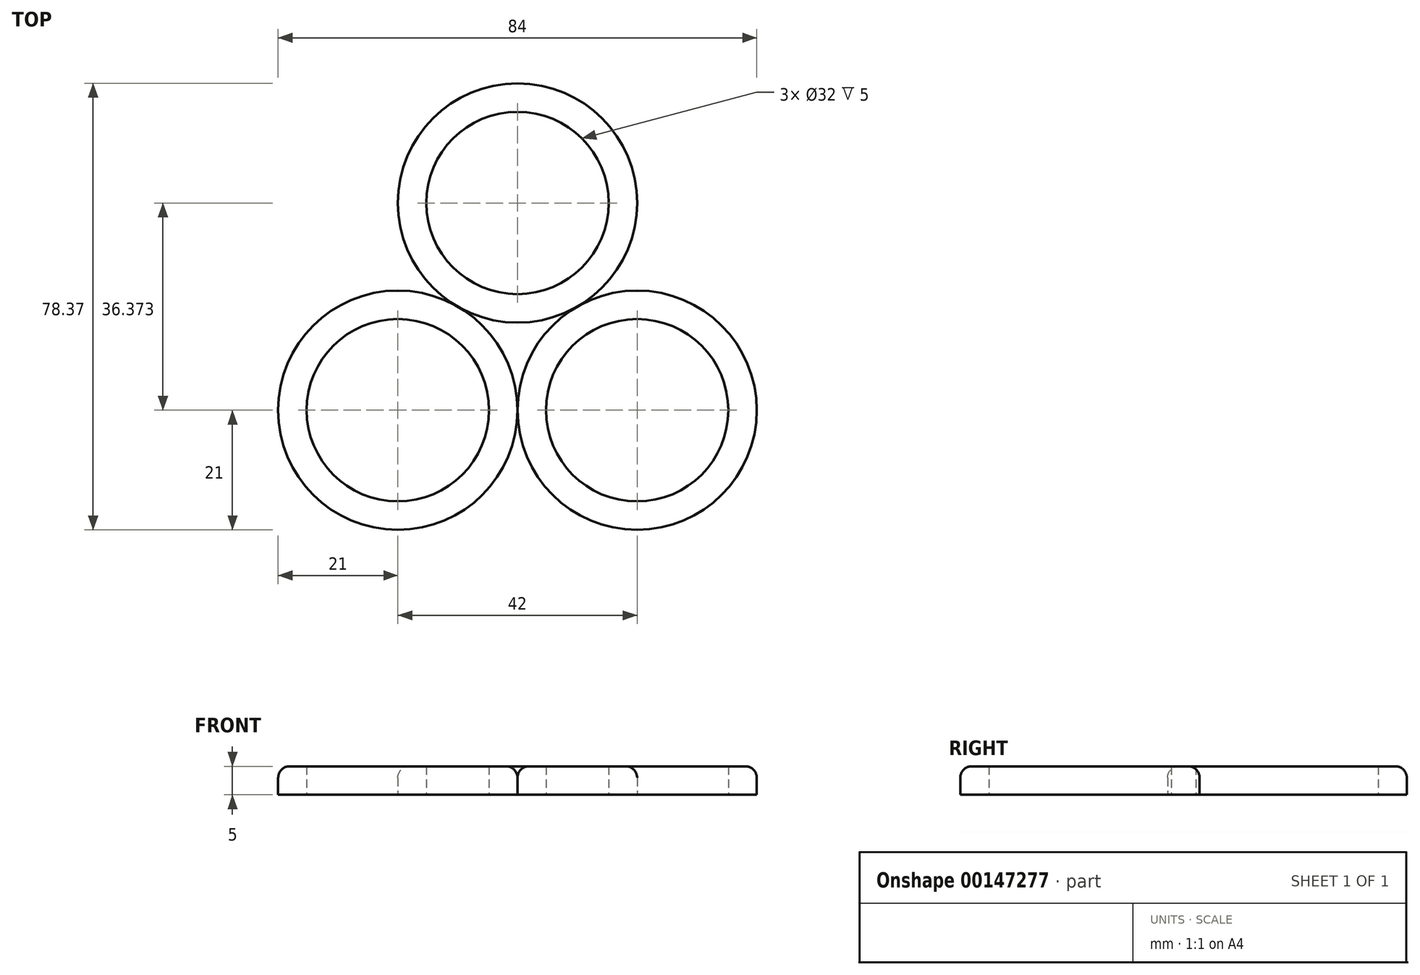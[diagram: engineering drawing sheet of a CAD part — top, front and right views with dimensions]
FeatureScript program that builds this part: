
annotation { "Feature Type Name" : "Feature", "Feature Type Description" : "" }
export const myFeature = defineFeature(function(context is Context, id is Id, definition is map)
    precondition{}
    {
        {
            var Q0;
            Q0=qCreatedBy(makeId("Top.planeOp"),FACE);
            var sketch = newSketch(context, id + "F0", { "sketchPlane" : qUnion([Q0])});
            skCircle(sketch, "E0", {"center": v(0, 0) * mm, "radius": 16 * mm});
            skCircle(sketch, "E1.0", {"center": v(0, 0) * mm, "radius": 21 * mm});
            skCircle(sketch, "E2", {"center": v(-42, 0) * mm, "radius": 16 * mm});
            skCircle(sketch, "E3.0", {"center": v(-42, 0) * mm, "radius": 21 * mm});
            skLineSegment(sketch, "E4", {"start": v(-42, 0) * mm, "end": v(-3, 67.56) * mm, "construction": true});
            skLineSegment(sketch, "E5", {"start": v(0, 0) * mm, "end": v(-38.06, 65.92) * mm, "construction": true});
            skCircle(sketch, "E6", {"center": v(-21, 36.37) * mm, "radius": 21 * mm});
            skCircle(sketch, "E7.0", {"center": v(-21, 36.37) * mm, "radius": 16 * mm});
            skLineSegment(sketch, "E8", {"start": v(36.37, -21) * mm, "end": v(-21, 78.37) * mm});
            skLineSegment(sketch, "E9", {"start": v(36.37, -21) * mm, "end": v(-78.37, -21) * mm});
            skLineSegment(sketch, "E10", {"start": v(-78.37, -21) * mm, "end": v(-21, 78.37) * mm});
            skPoint(sketch, "E11", {"position": v(-78.37, -21) * mm});
            skPoint(sketch, "E12", {"position": v(-21, 78.37) * mm});
            skPoint(sketch, "E13", {"position": v(36.37, -21) * mm});
            skSolve(sketch);
        }
        {
            var Q0;
            Q0=makeQuery(id+"F0.imprint","IMPRINT",FACE,{"disambiguationData":[TD([[makeQuery(id+"F0.imprint","IMPRINT",EDGE,{"derivedFrom":sQuery(id+"F0.wireOp",EDGE,"E2")}),-1.0]])]});
            var Q1;
            Q1=makeQuery(id+"F0.imprint","IMPRINT",FACE,{"disambiguationData":[TD([[makeQuery(id+"F0.imprint","IMPRINT",EDGE,{"derivedFrom":sQuery(id+"F0.wireOp",EDGE,"E0")}),-1.0]])]});
            var Q2;
            Q2=makeQuery(id+"F0.imprint","IMPRINT",FACE,{"disambiguationData":[TD([[makeQuery(id+"F0.imprint","IMPRINT",EDGE,{"derivedFrom":sQuery(id+"F0.wireOp",EDGE,"E7.0")}),-1.0]])]});
            extrude(context, id + "F1", {"entities" : qUnion([Q0, Q1, Q2]), "depth" : 5 * mm});
        }
        {
            var Q0;
            Q0=makeQuery(id+"F1.opExtrude","CAP_EDGE",EDGE,{"disambiguationData":[OSD([sQuery(id+"F0.wireOp",EDGE,"E3.0")])],"isStart":false});
            var Q1;
            Q1=makeQuery(id+"F1.opExtrude","CAP_EDGE",EDGE,{"disambiguationData":[OSD([sQuery(id+"F0.wireOp",EDGE,"E1.0")])],"isStart":false});
            var Q2;
            Q2=makeQuery(id+"F1.opExtrude","CAP_EDGE",EDGE,{"disambiguationData":[OSD([sQuery(id+"F0.wireOp",EDGE,"E6")])],"isStart":false});
            fillet(context, id + "F2", {"entities" : qUnion([Q0, Q1, Q2]), "radius" : 2 * mm, "tangentPropagation" : true, "allowEdgeOverflow" : false});
        }
    });
